# Revit family: KDW030061
name_source: partatom
category: Plumbing Fixtures
revit_build: Autodesk Revit 2015 (Build: 20140606_1530(x64)
units: mm (PartAtom-declared; Revit-internal decimal feet)

## types (1)
- KDW030061
    Additional features of the object = https://www.kaldewei.co.uk
    BIMobject category = Basins
    Brand url = http://www.kaldewei.com
    Color = https://www.kaldewei.co.uk
    ColourOptions = https://www.kaldewei.co.uk
    Configurator link = https://www.kaldewei.co.uk
    Description details = KALDEWEI international Worldwide partner for iconic bathroom solutions made of KALDEWEI steel enamel  KALDEWEI steel enamel delivers unique advantages that inspire excellence in bathroom design. Projects across the world, from upmarket hotels to private homes, capture the sophisticated aesthetic that recommends KALDEWEI as the partner of choice. As a leading international manufacturer of high-quality shower surfaces, bathtubs and washbasins made of superior steel enamel, KALDEWEI today is present in more than 80 countries.
    Design country = Germany
    Durability = https://EN 14688
    Edition number = 1
    Finish = Kaldewei
Kaldewei
Kaldewei
Kaldewei
    IFC Classification = Furnishing Element
    IfcExportAs = WASHHANDBASIN
    IfcExportType = IfcSanitaryTerminalType
    Link towards a photo of the product = https://www.kaldewei.co.uk
    Manufacturer country = Germany
    ManufacturerCountry = GERMANY
    ManufacturerName = KALDEWEI
    Material = steel enamel
    Material main = Steel
    Material secondary = Enamel
    NBS Reference Code = 35-65-70-94
    NBS Reference Description = Wash Basin Systems
    Name = CONO Handrinse washbasin
    Nominal height = 550 cm
    Nominal width = 300 cm
    ObjectName = CONO Handrinse washbasin 300x550
    ObjectNorm = EN 14688 EU DECLARATION OF PERFORMANCE (https://www.kaldewei.de
    Polantis code = KDW030061
    Product Guid = f1b576a8-52fb-44bf-ae1f-4b6cbdbcbbbe
    Product SKU = 3073
    Product certification = https://www.kaldewei.co.uk
    Product data url = https://bimobject.com
    Product family = CONO
    Product group = Washbasin
    Product url = https://www.kaldewei.co.uk
    ProductInformation = Model No. 3073: Two years ago, matching washbasins were added to the CONO product family.  The quality, and the consistent design and material make the bathroom into something truly special. Now the CONO line goes further, this time in the guest bathroom – in a space where an ultra compact hand-wash basin indicates that while the space may be limited, the guest is greatly appreciated. The CONO hand-wash basin is available in two versions with the tap panel to the left or right, and an option of 1 or no tap hole.
    QR code = http://bimobject.com
    SerialNumber = 3073
    Shape = Handbasin
    Size = 300x550
    Sound Insulation = DIN 4109:2016, VDI4100:2012
    Sustainability = https://EN 15804
    Technical data link = https://kaldewei.typo-live.web-factory.de
    Technical description = https://www.kaldewei.co.uk
    Type of accessories = https://www.kaldewei.co.uk
    Type of support framing = https://www.kaldewei.co.uk
    UNSPSC Code = 301815
    UNSPSCCode = 30181504
    UNSPSCNames = Sinks
    URL = https://www.kaldewei.com
    Uniclass 1.4 Code = L7212
    Uniclass 1.4 Description = Washbasins
    Uniclass 2.0 Code = SS-35-65-70-94
    Uniclass 2.0 Description = Wash Basin Systems
    Uniclass2 = Pr_40_20_96
    Version = 3
    WarrantyDurationParts = 30
    WarrantyDurationUnit = Year
    WarrantyStartDate = https://www.kaldewei.co.uk
    Website link = https://www.kaldewei.co.uk
    Weight = 8.2
    Weight Net (Kg) = 8.2

## geometry (parser evidence)
native form markers: Sweep x6
no freeform markers — native parametric forms only
